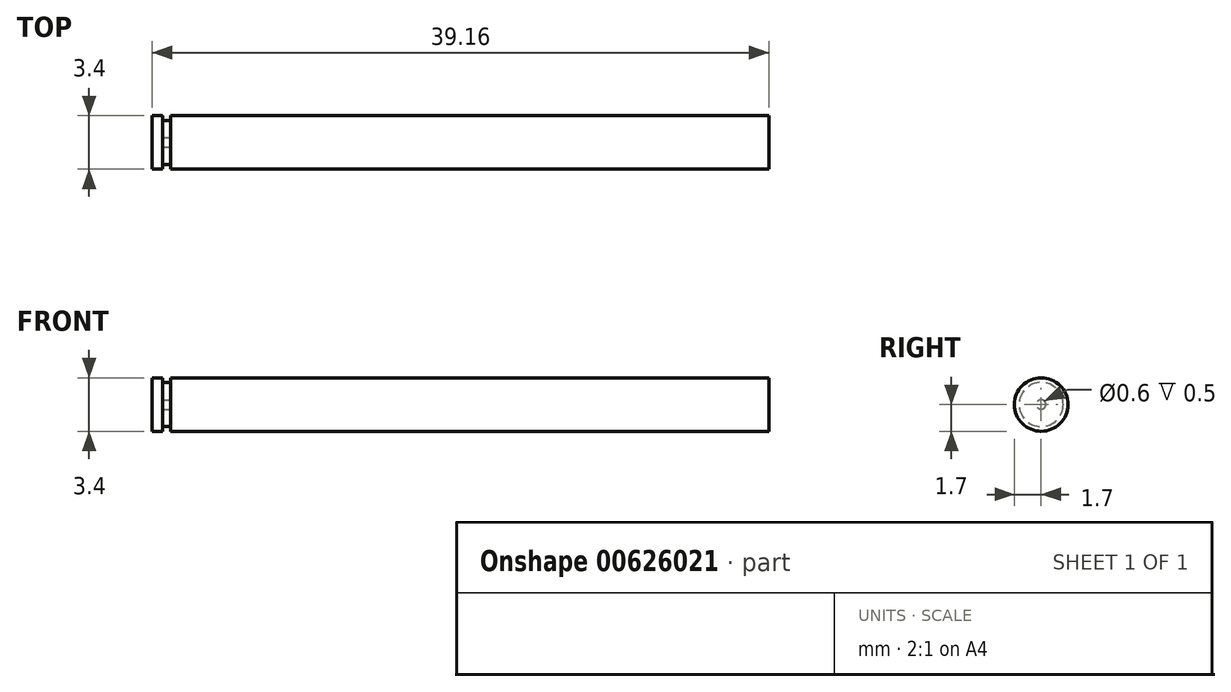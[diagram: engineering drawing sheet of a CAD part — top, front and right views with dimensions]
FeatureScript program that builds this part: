
annotation { "Feature Type Name" : "Feature", "Feature Type Description" : "" }
export const myFeature = defineFeature(function(context is Context, id is Id, definition is map)
    precondition{}
    {
        {
            var Q0;
            Q0=qCreatedBy(makeId("Front.planeOp"),FACE);
            var sketch = newSketch(context, id + "F0", { "sketchPlane" : qUnion([Q0])});
            skLineSegment(sketch, "E0.bottom", {"start": v(19, -0.85) * mm, "end": v(-19, -0.85) * mm});
            skLineSegment(sketch, "E0.top", {"start": v(19, 0.85) * mm, "end": v(-19, 0.85) * mm});
            skLineSegment(sketch, "E0.left", {"start": v(19, -0.85) * mm, "end": v(19, 0.85) * mm});
            skLineSegment(sketch, "E0.right", {"start": v(-19, -0.85) * mm, "end": v(-19, 0.85) * mm});
            skPoint(sketch, "E0.middle", {"position": v(0, 0) * mm});
            skLineSegment(sketch, "E1", {"start": v(-19, 0.55) * mm, "end": v(-19.5, 0.55) * mm});
            skLineSegment(sketch, "E2", {"start": v(-19, -0.55) * mm, "end": v(-19.5, -0.55) * mm});
            skLineSegment(sketch, "E3", {"start": v(-19.5, 0.55) * mm, "end": v(-19.5, 0.85) * mm});
            skLineSegment(sketch, "E4", {"start": v(-19.5, 0.85) * mm, "end": v(-20.16, 0.85) * mm});
            skLineSegment(sketch, "E5", {"start": v(-20.16, 0.85) * mm, "end": v(-20.16, -0.85) * mm});
            skLineSegment(sketch, "E6", {"start": v(-20.16, -0.85) * mm, "end": v(-19.5, -0.85) * mm});
            skLineSegment(sketch, "E7", {"start": v(-19.5, -0.85) * mm, "end": v(-19.5, -0.55) * mm});
            skSolve(sketch);
        }
        {
            var Q0;
            {var subQ1=sQuery(id+"F0.wireOp",EDGE,"E0.bottom");Q0=makeQuery(id+"F0.imprint","IMPRINT",FACE,{"disambiguationData":[TD([[makeQuery(id+"F0.imprint","IMPRINT",EDGE,{"derivedFrom":subQ1}),-1.0]])]});}
            var Q1;
            {var subQ1=sQuery(id+"F0.wireOp",EDGE,"E1");Q1=makeQuery(id+"F0.imprint","IMPRINT",FACE,{"disambiguationData":[TD([[makeQuery(id+"F0.imprint","IMPRINT",EDGE,{"derivedFrom":subQ1}),1.0]])]});}
            var Q2;
            Q2=sQuery(id+"F0.wireOp",EDGE,"E0.bottom");
            revolve(context, id + "F1", {"surfaceOperationType" : NewSurfaceOperationType.NEW, "entities" : qUnion([Q0, Q1]), "axis" : qUnion([Q2]), "revolveType" : RevolveType.FULL});
        }
    });
